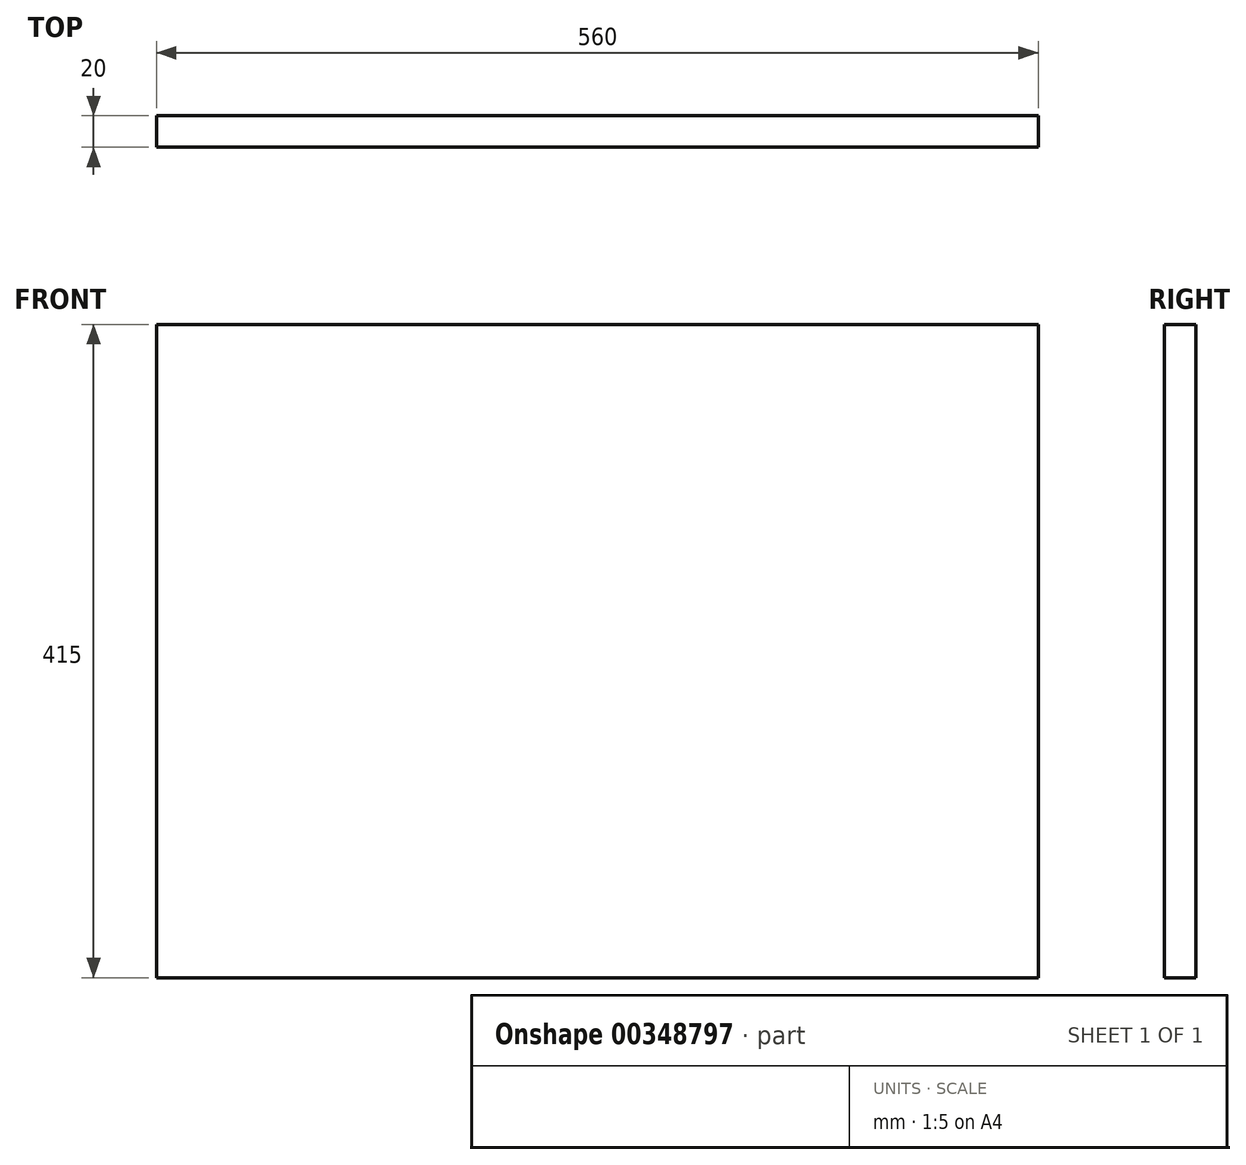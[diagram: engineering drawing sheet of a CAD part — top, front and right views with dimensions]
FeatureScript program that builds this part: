
annotation { "Feature Type Name" : "Feature", "Feature Type Description" : "" }
export const myFeature = defineFeature(function(context is Context, id is Id, definition is map)
    precondition{}
    {
        {
            var Q0;
            Q0=qCreatedBy(makeId("Front.planeOp"),FACE);
            var sketch = newSketch(context, id + "F0", { "sketchPlane" : qUnion([Q0])});
            skLineSegment(sketch, "E0.bottom", {"start": v(-560, -415) * mm, "end": v(0, -415) * mm});
            skLineSegment(sketch, "E0.top", {"start": v(-560, 0) * mm, "end": v(0, 0) * mm});
            skLineSegment(sketch, "E0.left", {"start": v(-560, -415) * mm, "end": v(-560, 0) * mm});
            skLineSegment(sketch, "E0.right", {"start": v(0, -415) * mm, "end": v(0, 0) * mm});
            skSolve(sketch);
        }
        {
            var Q0;
            Q0=qSketchRegion(id+"F0",true);
            extrude(context, id + "F1", {"entities" : qUnion([Q0]), "depth" : 20 * mm});
        }
    });
